# Revit family: LAC-CloudCover
name_source: partatom
category: Lighting Fixtures
revit_build: Autodesk Revit 2014 (Build: 20130709_2115(x64)
units: mm (PartAtom-declared; Revit-internal decimal feet)

## types (2) — shared parameters
Color Filter = 16777215
Comments = This model is for use in spatial massing and rendering. Please contact LightArt for pick-point placement and installation details.
Diffuser = White Opal Acrylic
Dimming Compatibility = 0-10v
Dimming Lamp Color Temperature Shift = <None>
Driver = 24v
Emit Shape Visible in Rendering = No
HARDWARE = Matte silver canopy mounts to round
junction box (provided by others)
(4) Stainless steel cables to ceiling
Silver power cord to canopy
Adjustable 12”-96” suspension
(4) Decorative caps visible on bottom
Hardware = Stainless Steel Cables
Input = 120v-277v
Light Source Symbol Size = 0' - 4"
Manufacturer = LightArt
Model = LAC-CloudCover
STANDARDS = Customizable dimensions, materials,
hardware and lighting
4-6 week lead time
10,000+ 3form material options
1 year limited warranty
Pricing based on maximum sheet yield and
Translucent Suede Varia material
Contact for custom pricing

## per-type parameters (varying)
| type | 20" x 40" x 8"H | Emit from Rectangle Length | Emit from Rectangle Width | Height From Face | LIGHTING | Shade |
| 20" x 20" x 8"H | No | 1' - 4" | 1' - 4" | 3' - 0" | Solid State LED System
120V-277V input; 24V driver;
0-10V dimming compatible
3000K 81 CRI light source
Dimming option available
UL compliant components
2700K 82 CRI light source
120V standard; 277V option available
LED option available
Dimming option available
UL Labeled | Shade |
| 20" x40" x 8"H | Yes | 3' - 4" | 1' - 2" | 5' - 0" | Solid State LED System
120V-277V input; 24V driver;
0-10V dimming compatible
3000K 81 CRI light source
Dimming option available
UL compliant components | <By Category> |

type visibility flags (boolean, named after types; folded from table):
- 20" x 20" x 8"H: Yes: 20" x 20" x 8"H
- 20" x40" x 8"H: Yes: (none)

## geometry (parser evidence)
native form markers: Blend x2, Sweep x13
no freeform markers — native parametric forms only
